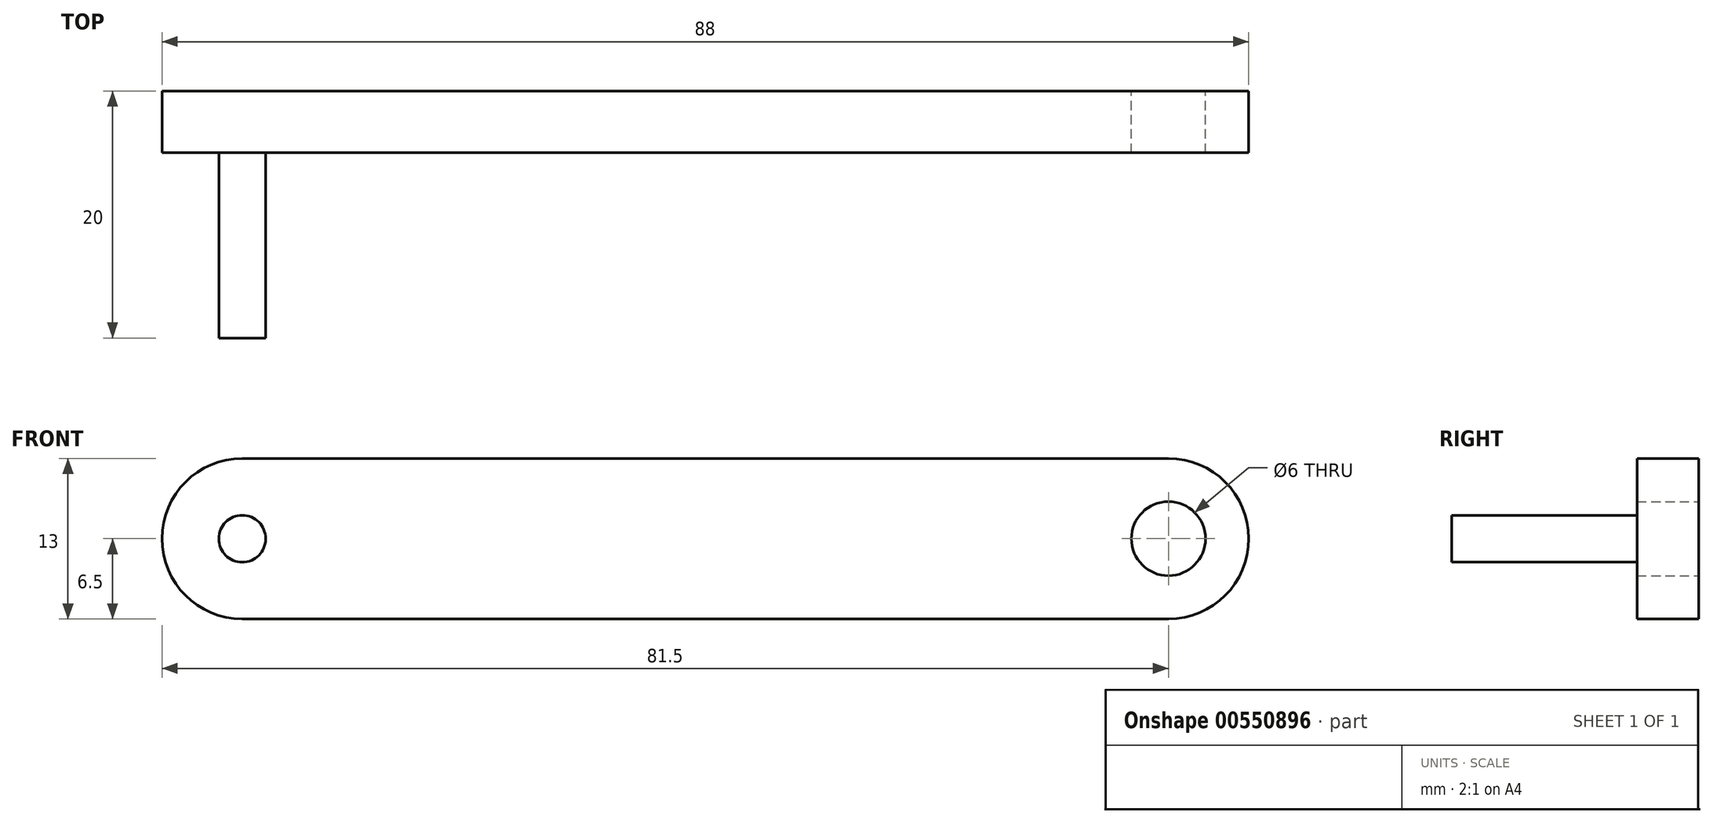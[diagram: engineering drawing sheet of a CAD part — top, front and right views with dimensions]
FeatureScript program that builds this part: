
annotation { "Feature Type Name" : "Feature", "Feature Type Description" : "" }
export const myFeature = defineFeature(function(context is Context, id is Id, definition is map)
    precondition{}
    {
        {
            var Q0;
            Q0=qCreatedBy(makeId("Front.planeOp"),FACE);
            var sketch = newSketch(context, id + "F0", { "sketchPlane" : qUnion([Q0])});
            skLineSegment(sketch, "E0", {"start": v(0, 6.5) * mm, "end": v(75, 6.5) * mm});
            skLineSegment(sketch, "E1", {"start": v(75, -6.5) * mm, "end": v(0, -6.5) * mm});
            skArc(sketch, "E2", {"start": v(0, 6.5) * mm, "mid": v(-6.5, 0) * mm, "end": v(0, -6.5) * mm});
            skArc(sketch, "E3", {"start": v(75, -6.5) * mm, "mid": v(81.5, 0) * mm, "end": v(75, 6.5) * mm});
            skCircle(sketch, "E4", {"center": v(75, 0) * mm, "radius": 3 * mm});
            skSolve(sketch);
        }
        {
            var Q0;
            Q0 = qSketchRegion(id + "F0", true);
            extrude(context, id + "F1", {"entities" : qUnion([Q0]), "depth" : 5 * mm, "offsetDistance" : 25 * mm});
        }
        {
            var Q0;
            Q0=makeQuery(id+"F1.opExtrude","CAP_FACE",FACE,{"disambiguationData":[OSD([sQuery(id+"F0.wireOp",EDGE,"E0"),sQuery(id+"F0.wireOp",EDGE,"E1"),sQuery(id+"F0.wireOp",EDGE,"E2"),sQuery(id+"F0.wireOp",EDGE,"E3"),sQuery(id+"F0.wireOp",EDGE,"E4")])],"isStart":false});
            var sketch = newSketch(context, id + "F2", { "sketchPlane" : qUnion([Q0])});
            skCircle(sketch, "E5", {"center": v(0, 0) * mm, "radius": 1.9 * mm});
            skSolve(sketch);
        }
        {
            var Q0;
            Q0 = qSketchRegion(id + "F2", true);
            extrude(context, id + "F3", {"entities" : qUnion([Q0]), "operationType" : NewBodyOperationType.ADD, "depth" : 15 * mm, "offsetDistance" : 25 * mm});
        }
    });
